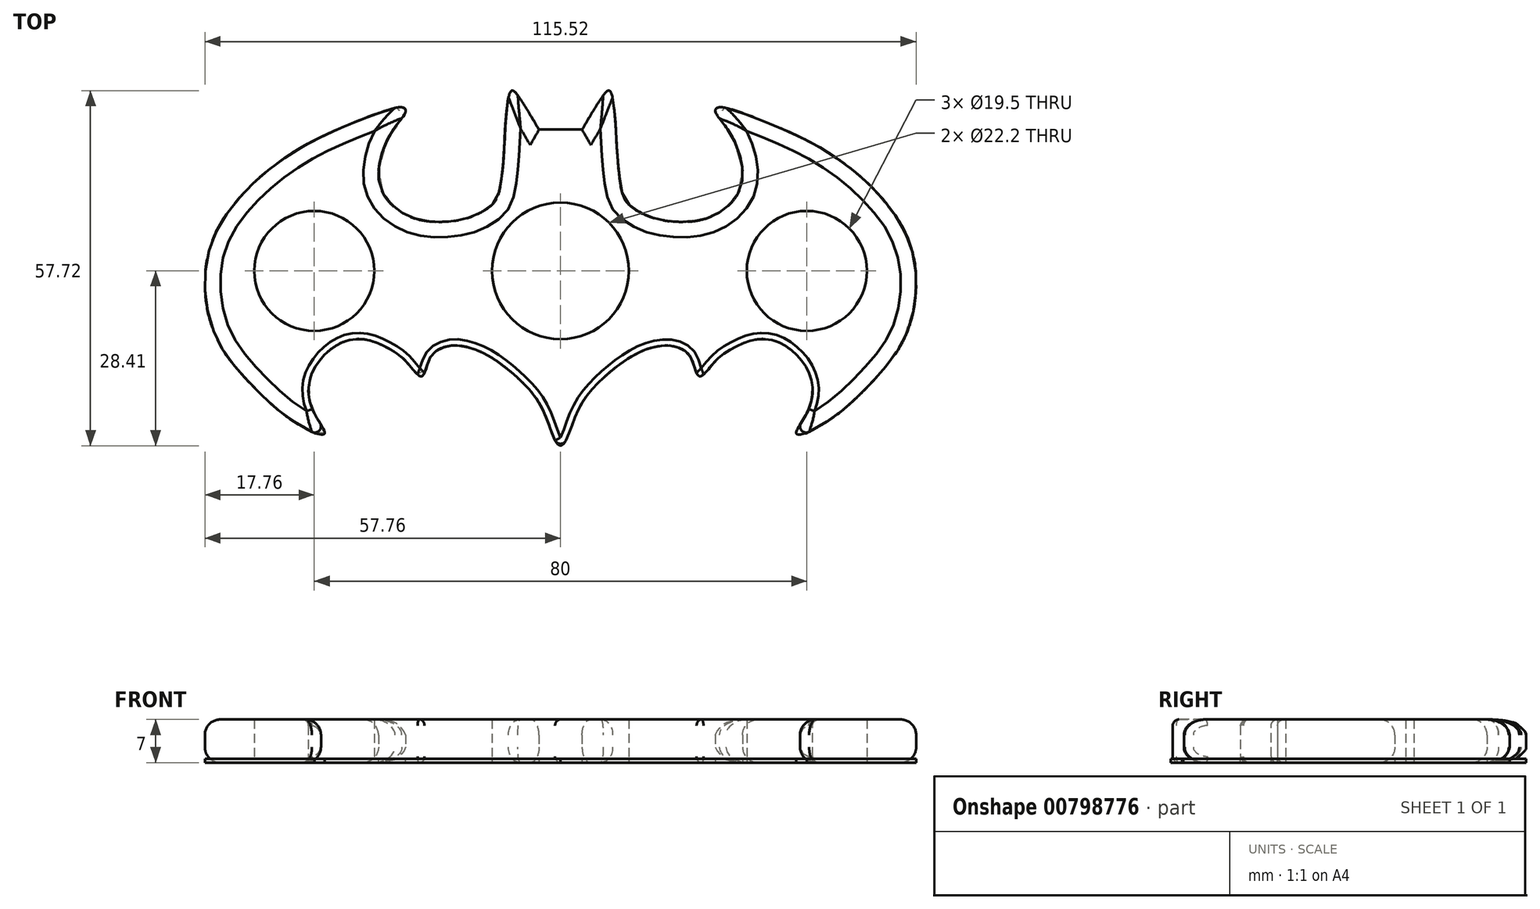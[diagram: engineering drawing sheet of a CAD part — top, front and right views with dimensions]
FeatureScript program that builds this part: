
annotation { "Feature Type Name" : "Feature", "Feature Type Description" : "" }
export const myFeature = defineFeature(function(context is Context, id is Id, definition is map)
    precondition{}
    {
        {
            var Q0;
            Q0=qCreatedBy(makeId("Top.planeOp"),FACE);
            var sketch = newSketch(context, id + "F0", { "sketchPlane" : qUnion([Q0])});
            skCircle(sketch, "E0", {"center": v(0, 0) * mm, "radius": 11.1 * mm});
            skLineSegment(sketch, "E1", {"start": v(0, 0) * mm, "end": v(-40, 0) * mm});
            skCircle(sketch, "E2", {"center": v(-40, 0) * mm, "radius": 9.75 * mm});
            skFitSpline(sketch, "E3", {"points": [v(0, -28.41) * mm, v(-0.69, -27.9) * mm, v(-2.81, -22.69) * mm, v(-6.63, -17.7) * mm, v(-12.36, -13.44) * mm, v(-17.05, -12.12) * mm, v(-19.7, -12.7) * mm, v(-21.3, -14.4) * mm, v(-22.56, -17.11) * mm, v(-24.98, -14.84) * mm, v(-27.99, -12.56) * mm, v(-31.29, -11.24) * mm, v(-34.6, -11.31) * mm, v(-37.45, -12.86) * mm, v(-39.46, -14.98) * mm, v(-40.87, -18.37) * mm, v(-39.98, -23.18) * mm, v(-38.3, -26.44) * mm, v(-39.98, -26.38) * mm], "startDerivative": vector(-24.95, 9.98) * mm, "endDerivative": vector(-59.97, 13.63) * mm});
            skFitSpline(sketch, "E4", {"points": [v(-39.98, -26.38) * mm, v(-45.16, -23.18) * mm, v(-51.3, -17.3) * mm, v(-55.01, -12.54) * mm, v(-57.2, -7.05) * mm, v(-57.76, -1.56) * mm, v(-57.21, 2.8) * mm, v(-54.9, 8.28) * mm, v(-50.25, 13.9) * mm, v(-47.17, 16.6) * mm, v(-43.65, 19.14) * mm, v(-39.21, 21.61) * mm, v(-34.36, 23.79) * mm, v(-29.12, 25.81) * mm, v(-25.6, 26.56) * mm, v(-25.15, 25.96) * mm, v(-27.17, 22.96) * mm, v(-29.34, 17.8) * mm, v(-29.34, 13.9) * mm, v(-27.92, 11.27) * mm, v(-25.52, 9.33) * mm, v(-22.45, 8.2) * mm, v(-19.15, 7.98) * mm, v(-15.63, 8.43) * mm, v(-12.56, 9.7) * mm, v(-10.61, 11.35) * mm, v(-9.86, 13.37) * mm, v(-9.19, 19.37) * mm, v(-7.99, 29.26) * mm, v(-6.72, 28.2) * mm, v(-3.5, 22.96) * mm], "startDerivative": vector(-130.4, 70) * mm, "endDerivative": vector(86.6, -147.2) * mm});
            skLineSegment(sketch, "E5", {"start": v(-3.5, 22.96) * mm, "end": v(0, 22.96) * mm});
            skFitSpline(sketch, "E6.MirrorCS", {"points": [v(39.98, -26.38) * mm, v(45.16, -23.18) * mm, v(51.3, -17.3) * mm, v(55.01, -12.54) * mm, v(57.2, -7.05) * mm, v(57.76, -1.56) * mm, v(57.21, 2.8) * mm, v(54.9, 8.28) * mm, v(50.25, 13.9) * mm, v(47.17, 16.6) * mm, v(43.65, 19.14) * mm, v(39.21, 21.61) * mm, v(34.36, 23.79) * mm, v(29.12, 25.81) * mm, v(25.6, 26.56) * mm, v(25.15, 25.96) * mm, v(27.17, 22.96) * mm, v(29.34, 17.8) * mm, v(29.34, 13.9) * mm, v(27.92, 11.27) * mm, v(25.52, 9.33) * mm, v(22.45, 8.2) * mm, v(19.15, 7.98) * mm, v(15.63, 8.43) * mm, v(12.56, 9.7) * mm, v(10.61, 11.35) * mm, v(9.86, 13.37) * mm, v(9.19, 19.37) * mm, v(7.99, 29.26) * mm, v(6.72, 28.2) * mm, v(3.5, 22.96) * mm], "startDerivative": vector(130.4, 70) * mm, "endDerivative": vector(-86.6, -147.2) * mm});
            skFitSpline(sketch, "E7.MirrorCS", {"points": [v(0, -28.41) * mm, v(0.69, -27.9) * mm, v(2.81, -22.69) * mm, v(6.63, -17.7) * mm, v(12.36, -13.44) * mm, v(17.05, -12.12) * mm, v(19.7, -12.7) * mm, v(21.3, -14.4) * mm, v(22.56, -17.11) * mm, v(24.98, -14.84) * mm, v(27.99, -12.56) * mm, v(31.29, -11.24) * mm, v(34.6, -11.31) * mm, v(37.45, -12.86) * mm, v(39.46, -14.98) * mm, v(40.87, -18.37) * mm, v(39.98, -23.18) * mm, v(38.3, -26.44) * mm, v(39.98, -26.38) * mm], "startDerivative": vector(24.95, 9.98) * mm, "endDerivative": vector(59.97, 13.63) * mm});
            skCircle(sketch, "E8.MirrorC", {"center": v(40, 0) * mm, "radius": 9.75 * mm});
            skLineSegment(sketch, "E9", {"start": v(0, 22.96) * mm, "end": v(3.5, 22.96) * mm});
            skSolve(sketch);
        }
        {
            var Q0;
            Q0=makeQuery(id+"F0.imprint","IMPRINT",FACE,{"disambiguationData":[TD([[makeQuery(id+"F0.imprint","IMPRINT",EDGE,{"derivedFrom":sQuery(id+"F0.wireOp",EDGE,"E2")}),1.0]])]});
            var Q1;
            Q1=makeQuery(id+"F0.imprint","IMPRINT",FACE,{"disambiguationData":[TD([[makeQuery(id+"F0.imprint","IMPRINT",EDGE,{"derivedFrom":sQuery(id+"F0.wireOp",EDGE,"E8.MirrorC")}),-1.0]])]});
            extrude(context, id + "F1", {"entities" : qUnion([Q0, Q1]), "depth" : .6 * mm, "offsetDistance" : 25 * mm});
        }
        {
            var Q0;
            Q0=makeQuery(id+"F0.imprint","IMPRINT",FACE,{"disambiguationData":[TD([[makeQuery(id+"F0.imprint","IMPRINT",EDGE,{"derivedFrom":sQuery(id+"F0.wireOp",EDGE,"E0")}),-1.0]])]});
            extrude(context, id + "F2", {"entities" : qUnion([Q0]), "depth" : 7 * mm, "offsetDistance" : 25 * mm});
        }
        {
            var Q0;
            Q0=makeQuery(id+"F2.opExtrude","CAP_EDGE",EDGE,{"disambiguationData":[OSD([sQuery(id+"F0.wireOp",EDGE,"E4")])],"isStart":false});
            var Q1;
            Q1=makeQuery(id+"F2.opExtrude","CAP_EDGE",EDGE,{"disambiguationData":[OSD([sQuery(id+"F0.wireOp",EDGE,"E6.MirrorCS")])],"isStart":false});
            var Q2;
            Q2=makeQuery(id+"F2.opExtrude","CAP_EDGE",EDGE,{"disambiguationData":[OSD([sQuery(id+"F0.wireOp",EDGE,"E5"),sQuery(id+"F0.wireOp",EDGE,"E9")])],"isStart":false});
            var Q3;
            Q3=makeQuery(id+"F2.opExtrude","CAP_EDGE",EDGE,{"disambiguationData":[OSD([sQuery(id+"F0.wireOp",EDGE,"E4")])],"isStart":true});
            var Q4;
            Q4=makeQuery(id+"F2.opExtrude","CAP_EDGE",EDGE,{"disambiguationData":[OSD([sQuery(id+"F0.wireOp",EDGE,"E5"),sQuery(id+"F0.wireOp",EDGE,"E9")])],"isStart":true});
            var Q5;
            Q5=makeQuery(id+"F2.opExtrude","CAP_EDGE",EDGE,{"disambiguationData":[OSD([sQuery(id+"F0.wireOp",EDGE,"E6.MirrorCS")])],"isStart":true});
            fillet(context, id + "F3", {"entities" : qUnion([Q0, Q1, Q2, Q3, Q4, Q5]), "radius" : 2.5 * mm, "tangentPropagation" : true, "allowEdgeOverflow" : false});
        }
        {
            var Q0;
            Q0=makeQuery(id+"F2.opExtrude","CAP_EDGE",EDGE,{"disambiguationData":[OSD([sQuery(id+"F0.wireOp",EDGE,"E3"),sQuery(id+"F0.wireOp",EDGE,"E3")])],"isStart":false});
            fillet(context, id + "F4", {"entities" : qUnion([Q0]), "radius" : 1 * mm, "tangentPropagation" : true, "allowEdgeOverflow" : false});
        }
        {
            var Q0;
            Q0=makeQuery(id+"F2.opExtrude","CAP_EDGE",EDGE,{"disambiguationData":[OSD([sQuery(id+"F0.wireOp",EDGE,"E7.MirrorCS")])],"isStart":false});
            fillet(context, id + "F5", {"entities" : qUnion([Q0]), "radius" : 1 * mm, "tangentPropagation" : true, "allowEdgeOverflow" : false});
        }
    });
